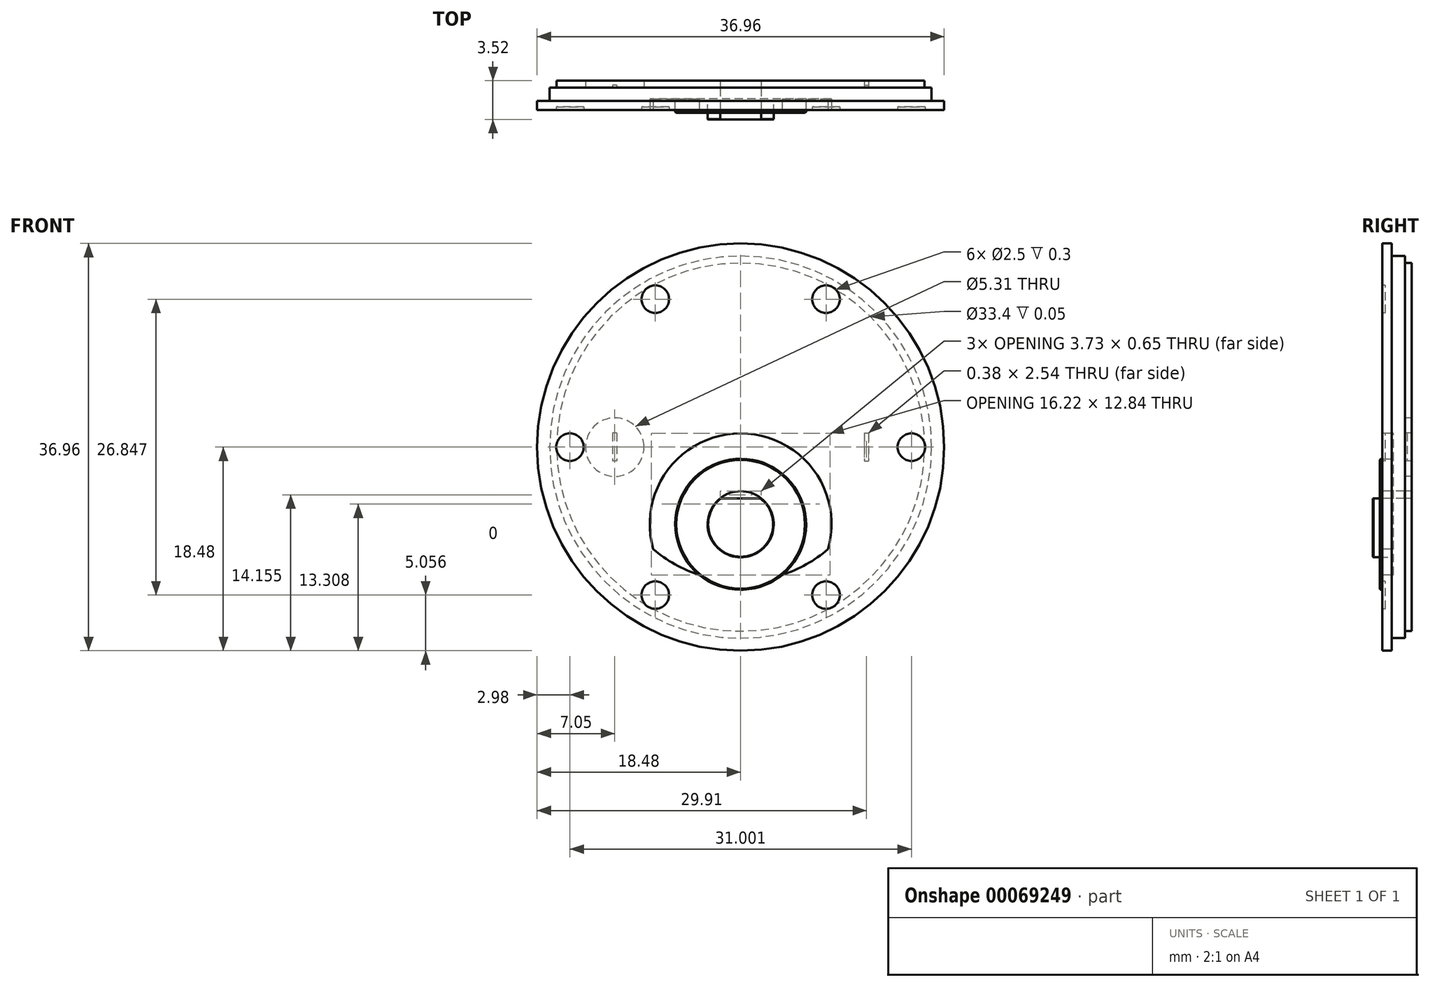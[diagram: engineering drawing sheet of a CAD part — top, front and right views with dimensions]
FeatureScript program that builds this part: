
annotation { "Feature Type Name" : "Feature", "Feature Type Description" : "" }
export const myFeature = defineFeature(function(context is Context, id is Id, definition is map)
    precondition{}
    {
        {
            assignVariable(context, id + "F0", {"name" : "body_length", "anyValue" : 1.21});
        }
        {
            var Q0;
            Q0=qCreatedBy(makeId("Front.planeOp"),FACE);
            var sketch = newSketch(context, id + "F1", { "sketchPlane" : qUnion([Q0])});
            skCircle(sketch, "E0", {"center": v(0, 0) * mm, "radius": 17.34 * mm});
            skSolve(sketch);
        }
        {
            var Q0;
            Q0=makeQuery(id+"F1.imprint","IMPRINT",FACE,{"disambiguationData":[TD([[makeQuery(id+"F1.imprint","IMPRINT",EDGE,{"derivedFrom":sQuery(id+"F1.wireOp",EDGE,"E0")}),1.0]])]});
            extrude(context, id + "F2", {"entities" : qUnion([Q0]), "oppositeDirection" : true, "depth" : (getVariable(context, 'body_length')) * mm});
        }
        {
            assignVariable(context, id + "F3", {"name" : "shell_relief", "anyValue" : 0.05});
        }
        {
            var Q0;
            Q0=makeQuery(id+"F2.opExtrude","CAP_FACE",FACE,{"disambiguationData":[OSD([sQuery(id+"F1.wireOp",EDGE,"E0")])],"isStart":false});
            var sketch = newSketch(context, id + "F4", { "sketchPlane" : qUnion([Q0])});
            skCircle(sketch, "E1.0", {"center": v(0, 0) * mm, "radius": 17.34 * mm});
            skCircle(sketch, "E2", {"center": v(0, 0) * mm, "radius": 16.7 * mm});
            skSolve(sketch);
        }
        {
            var Q0;
            Q0=makeQuery(id+"F4.imprint","IMPRINT",FACE,{"disambiguationData":[TD([[makeQuery(id+"F4.imprint","IMPRINT",EDGE,{"derivedFrom":sQuery(id+"F4.wireOp",EDGE,"E2")}),1.0]])]});
            extrude(context, id + "F5", {"entities" : qUnion([Q0]), "operationType" : NewBodyOperationType.REMOVE, "oppositeDirection" : true, "depth" : (getVariable(context, 'shell_relief')) * mm});
        }
        {
            assignVariable(context, id + "F6", {"name" : "gearbox_length", "anyValue" : 0.84});
        }
        {
            var Q0;
            Q0=qCreatedBy(makeId("Front.planeOp"),FACE);
            var sketch = newSketch(context, id + "F7", { "sketchPlane" : qUnion([Q0])});
            skCircle(sketch, "E3", {"center": v(0, 0) * mm, "radius": 18.48 * mm});
            skSolve(sketch);
        }
        {
            var Q0;
            Q0=makeQuery(id+"F7.imprint","IMPRINT",FACE,{"disambiguationData":[TD([[makeQuery(id+"F7.imprint","IMPRINT",EDGE,{"derivedFrom":sQuery(id+"F7.wireOp",EDGE,"E3")}),1.0]])]});
            extrude(context, id + "F8", {"entities" : qUnion([Q0]), "depth" : (getVariable(context, 'gearbox_length')) * mm});
        }
        {
            assignVariable(context, id + "F9", {"name" : "shoulder_length", "anyValue" : 0.23});
        }
        {
            var Q0;
            Q0=makeQuery(id+"F8.opExtrude","CAP_FACE",FACE,{"disambiguationData":[OSD([sQuery(id+"F7.wireOp",EDGE,"E3")])],"isStart":false});
            var sketch = newSketch(context, id + "F10", { "sketchPlane" : qUnion([Q0])});
            skPoint(sketch, "E4.0", {"position": v(0, 0) * mm});
            skCircle(sketch, "E5", {"center": v(0, -7) * mm, "radius": 5.94 * mm});
            skSolve(sketch);
        }
        {
            var Q0;
            Q0=makeQuery(id+"F10.imprint","IMPRINT",FACE,{"disambiguationData":[TD([[makeQuery(id+"F10.imprint","IMPRINT",EDGE,{"derivedFrom":sQuery(id+"F10.wireOp",EDGE,"E5")}),1.0]])]});
            extrude(context, id + "F11", {"entities" : qUnion([Q0]), "operationType" : NewBodyOperationType.ADD, "depth" : (getVariable(context, 'shoulder_length')) * mm});
        }
        {
            assignVariable(context, id + "F12", {"name" : "screw_hole_depth", "anyValue" : 0.3});
        }
        {
            var Q0;
            Q0=makeQuery(id+"F8.opExtrude","CAP_FACE",FACE,{"disambiguationData":[OSD([sQuery(id+"F7.wireOp",EDGE,"E3")])],"isStart":false});
            var sketch = newSketch(context, id + "F13", { "sketchPlane" : qUnion([Q0])});
            skCircle(sketch, "E6", {"center": v(0, 0) * mm, "radius": 15.5 * mm, "construction": true});
            skCircle(sketch, "E7", {"center": v(-15.5, 0) * mm, "radius": 1.25 * mm});
            skCircle(sketch, "E8.1.0", {"center": v(-7.75, -13.42) * mm, "radius": 1.25 * mm});
            skCircle(sketch, "E8.2.0", {"center": v(7.75, -13.42) * mm, "radius": 1.25 * mm});
            skCircle(sketch, "E8.3.0", {"center": v(15.5, 0) * mm, "radius": 1.25 * mm});
            skCircle(sketch, "E8.4.0", {"center": v(7.75, 13.42) * mm, "radius": 1.25 * mm});
            skCircle(sketch, "E8.5.0", {"center": v(-7.75, 13.42) * mm, "radius": 1.25 * mm});
            skSolve(sketch);
        }
        {
            var Q0;
            Q0=qSketchRegion(id+"F13",true);
            extrude(context, id + "F14", {"entities" : qUnion([Q0]), "operationType" : NewBodyOperationType.REMOVE, "oppositeDirection" : true, "depth" : (getVariable(context, 'screw_hole_depth')) * mm});
        }
        {
            var Q0;
            Q0=makeQuery(id+"F8.opExtrude","CAP_FACE",FACE,{"disambiguationData":[OSD([sQuery(id+"F7.wireOp",EDGE,"E3")])],"isStart":false});
            var sketch = newSketch(context, id + "F15", { "sketchPlane" : qUnion([Q0])});
            skCircle(sketch, "E9", {"center": v(0, 0) * mm, "radius": 12.2 * mm});
            skCircle(sketch, "E10.0", {"center": v(0, -7) * mm, "radius": 5.94 * mm});
            skCircle(sketch, "E11", {"center": v(0, -7) * mm, "radius": 8.25 * mm});
            skSolve(sketch);
        }
        {
            var Q0;
            {var subQ0=sQuery(id+"F15.wireOp",EDGE,"E11");var subQ1=sQuery(id+"F15.wireOp",EDGE,"E9");var subQ2=makeQuery(id+"F15.imprint","INTERSECT",VERTEX,{"disambiguationData":[OD(0.0)],"derivedFrom":[subQ1,subQ0]});Q0=makeQuery(id+"F15.imprint","IMPRINT",FACE,{"disambiguationData":[TD([[makeQuery(id+"F15.imprint","IMPRINT",EDGE,{"disambiguationData":[TD([[subQ2,1.0]])],"derivedFrom":subQ1}),1.0]])]});}
            extrude(context, id + "F16", {"entities" : qUnion([Q0]), "operationType" : NewBodyOperationType.REMOVE, "oppositeDirection" : true, "depth" : 1.02 * mm});
        }
        {
            assignVariable(context, id + "F17", {"name" : "shaft_length", "anyValue" : 0.62});
        }
        {
            var Q0;
            Q0=makeQuery(id+"F11.opExtrude","CAP_FACE",FACE,{"disambiguationData":[OSD([sQuery(id+"F10.wireOp",EDGE,"E5")])],"isStart":false});
            var sketch = newSketch(context, id + "F18", { "sketchPlane" : qUnion([Q0])});
            skCircle(sketch, "E12.0", {"center": v(0, -7) * mm, "radius": 5.94 * mm});
            skCircle(sketch, "E13", {"center": v(0, -7) * mm, "radius": 3 * mm});
            skSolve(sketch);
        }
        {
            var Q0;
            Q0=makeQuery(id+"F18.imprint","IMPRINT",FACE,{"disambiguationData":[TD([[makeQuery(id+"F18.imprint","IMPRINT",EDGE,{"derivedFrom":sQuery(id+"F18.wireOp",EDGE,"E13")}),1.0]])]});
            var Q1;
            Q1=makeQuery(id+"F2.opExtrude","SWEPT_BODY",BODY,{"disambiguationData":[OSD([sQuery(id+"F1.wireOp",EDGE,"E0")])]});
            extrude(context, id + "F19", {"entities" : qUnion([Q0]), "depth" : (getVariable(context, 'shaft_length')) * mm, "hasSecondDirection" : true, "secondDirectionBound" : SecondDirectionBoundingType.UP_TO_BODY, "secondDirectionOppositeDirection" : true, "secondDirectionBoundEntityBody" : qUnion([Q1]), "secondDirectionDepth" : 25.4 * mm});
        }
        {
            assignVariable(context, id + "F20", {"name" : "flat_length", "anyValue" : 12 * mm});
        }
        {
            var Q0;
            Q0=makeQuery(id+"F19.opExtrude","CAP_FACE",FACE,{"disambiguationData":[OSD([sQuery(id+"F18.wireOp",EDGE,"E13")])],"isStart":false});
            var sketch = newSketch(context, id + "F21", { "sketchPlane" : qUnion([Q0])});
            skLineSegment(sketch, "E14", {"start": v(-1.86, -4.65) * mm, "end": v(1.86, -4.65) * mm});
            skPoint(sketch, "E15", {"position": v(0, -10) * mm});
            skSolve(sketch);
        }
        {
            var Q0;
            {var subQ0=sQuery(id+"F21.wireOp",EDGE,"E14");Q0=makeQuery(id+"F21.imprint","IMPRINT",FACE,{"disambiguationData":[TD([[makeQuery(id+"F21.imprint","IMPRINT",EDGE,{"derivedFrom":subQ0}),1.0]])]});}
            extrude(context, id + "F22", {"entities" : qUnion([Q0]), "operationType" : NewBodyOperationType.REMOVE, "oppositeDirection" : true, "depth" : getVariable(context, 'flat_length')});
        }
        {
            assignVariable(context, id + "F23", {"name" : "shoulder_chamfer", "anyValue" : .1});
        }
        {
            var Q0;
            Q0=makeQuery(id+"F11.opExtrude","CAP_EDGE",EDGE,{"disambiguationData":[OSD([sQuery(id+"F10.wireOp",EDGE,"E5")])],"isStart":false});
            chamfer(context, id + "F24", {"entities" : qUnion([Q0]), "width" : (getVariable(context, 'shoulder_chamfer')) * mm, "tangentPropagation" : true});
        }
        {
            assignVariable(context, id + "F25", {"name" : "shaft_chamfer", "anyValue" : getVariable(context, 'shoulder_chamfer') / 2});
        }
        {
            var Q0;
            Q0=makeQuery(id+"F19.opExtrude","CAP_EDGE",EDGE,{"disambiguationData":[OSD([sQuery(id+"F18.wireOp",EDGE,"E13")])],"isStart":false});
            chamfer(context, id + "F26", {"entities" : qUnion([Q0]), "width" : (getVariable(context, 'shaft_chamfer')) * mm, "tangentPropagation" : true});
        }
        {
            assignVariable(context, id + "F27", {"name" : "tab_height", "anyValue" : 0.25});
        }
        {
            assignVariable(context, id + "F28", {"name" : "tab_shoulder_height", "anyValue" : .67});
        }
        {
            var Q0;
            Q0=makeQuery(id+"F5.boolean.opBoolean","COPY",FACE,{"derivedFrom":makeQuery(id+"F5.opExtrude","CAP_FACE",FACE,{"disambiguationData":[OSD([sQuery(id+"F4.wireOp",EDGE,"E2")])],"isStart":false})});
            var sketch = newSketch(context, id + "F29", { "sketchPlane" : qUnion([Q0])});
            skPoint(sketch, "E16.0", {"position": v(0, 0) * mm});
            skCircle(sketch, "E17", {"center": v(-11.43, 0) * mm, "radius": 2.65 * mm});
            skCircle(sketch, "E18.MirrorC", {"center": v(11.43, 0) * mm, "radius": 2.65 * mm});
            skLineSegment(sketch, "E19.rect.bottom", {"start": v(-11.24, 1.27) * mm, "end": v(-11.62, 1.27) * mm});
            skLineSegment(sketch, "E19.rect.top", {"start": v(-11.24, -1.27) * mm, "end": v(-11.62, -1.27) * mm});
            skLineSegment(sketch, "E19.rect.left", {"start": v(-11.24, 1.27) * mm, "end": v(-11.24, -1.27) * mm});
            skLineSegment(sketch, "E19.rect.right", {"start": v(-11.62, 1.27) * mm, "end": v(-11.62, -1.27) * mm});
            skLineSegment(sketch, "E20.MirrorCS", {"start": v(11.24, -1.27) * mm, "end": v(11.62, -1.27) * mm});
            skLineSegment(sketch, "E21.MirrorCS", {"start": v(11.24, 1.27) * mm, "end": v(11.62, 1.27) * mm});
            skLineSegment(sketch, "E22.MirrorCS", {"start": v(11.24, 1.27) * mm, "end": v(11.24, -1.27) * mm});
            skLineSegment(sketch, "E23.MirrorCS", {"start": v(11.62, 1.27) * mm, "end": v(11.62, -1.27) * mm});
            skSolve(sketch);
        }
        {
            var Q0;
            Q0=makeQuery(id+"F29.imprint","IMPRINT",FACE,{"disambiguationData":[TD([[makeQuery(id+"F29.imprint","IMPRINT",EDGE,{"derivedFrom":sQuery(id+"F29.wireOp",EDGE,"E17")}),1.0]])]});
            var Q1;
            Q1=makeQuery(id+"F29.imprint","IMPRINT",FACE,{"disambiguationData":[TD([[makeQuery(id+"F29.imprint","IMPRINT",EDGE,{"derivedFrom":sQuery(id+"F29.wireOp",EDGE,"E18.MirrorC")}),-1.0]])]});
            extrude(context, id + "F30", {"entities" : qUnion([Q0, Q1]), "depth" : (getVariable(context, 'tab_shoulder_height')) * mm});
        }
        {
            var Q0;
            Q0=makeQuery(id+"F29.imprint","IMPRINT",FACE,{"disambiguationData":[TD([[makeQuery(id+"F29.imprint","IMPRINT",EDGE,{"derivedFrom":sQuery(id+"F29.wireOp",EDGE,"E19.rect.bottom")}),1.0]])]});
            var Q1;
            Q1=makeQuery(id+"F29.imprint","IMPRINT",FACE,{"disambiguationData":[TD([[makeQuery(id+"F29.imprint","IMPRINT",EDGE,{"derivedFrom":sQuery(id+"F29.wireOp",EDGE,"E20.MirrorCS")}),1.0]])]});
            extrude(context, id + "F31", {"entities" : qUnion([Q0, Q1]), "depth" : (getVariable(context, 'tab_height')) * mm});
        }
    });
